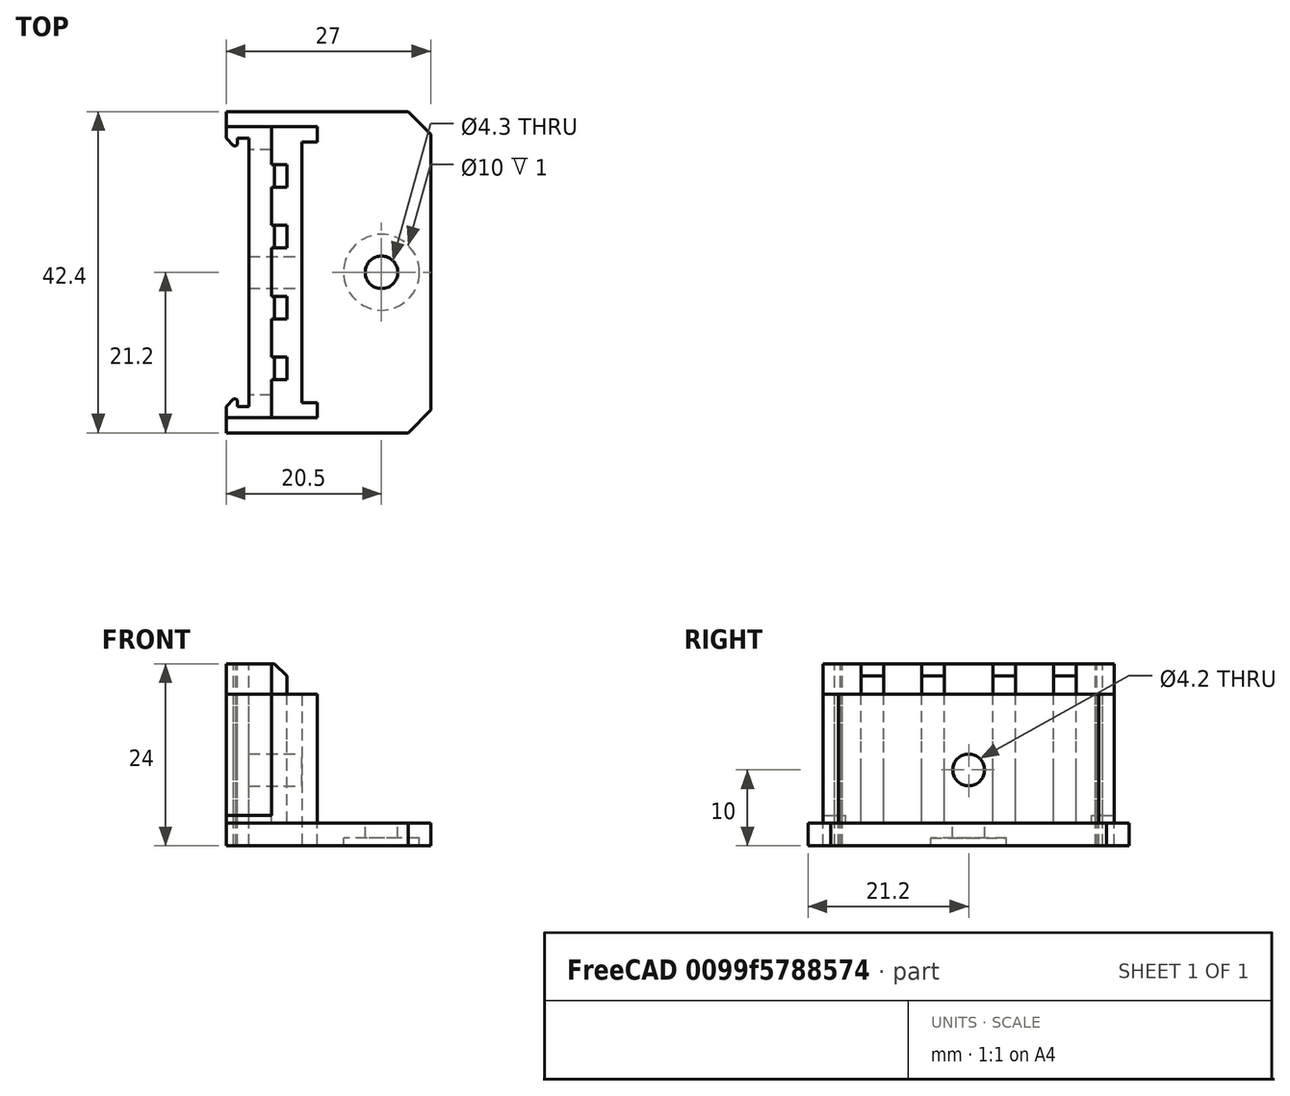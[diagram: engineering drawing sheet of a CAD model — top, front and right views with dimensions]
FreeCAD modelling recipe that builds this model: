
FCSTD DOCUMENT  (FreeCAD 0.18R16146 (Git))
Label: din-clip
License: All rights reserved
LicenseURL: http://en.wikipedia.org/wiki/All_rights_reserved
objects: Part::Box×15, Part::Chamfer×6, Part::Feature×5, Part::MultiFuse×4, Part::Cut×4, Part::Cylinder×3
note: 37 computed .brp shape members not serialized (recipe doc carries the construction recipe); baked Part::Feature solids carry a one-line shape summary decoded from their .brp

FEATURE [Part::Box] Box  label="Cube"
  AttacherType = Attacher::AttachEngine3D
  Height = 10
  Length = 3
  Width = 35.4
FEATURE [Part::Box] Box001  label="Cube001"
  AttacherType = Attacher::AttachEngine3D
  Height = 10
  Length = 6
  Placement = pos=(-3,-1.5,0) rot=(0,0,1;0rad)
  Width = 1.5
FEATURE [Part::Box] Box002  label="Cube002"
  AttacherType = Attacher::AttachEngine3D
  Height = 10
  Length = 6
  Placement = pos=(-3,35.4,0) rot=(0,0,1;0rad)
  Width = 1.5
FEATURE [Part::Box] Box003  label="Cube003"
  AttacherType = Attacher::AttachEngine3D
  Height = 10
  Length = 1.5
  Placement = pos=(-3,-1.5,0) rot=(0,0,1;0rad)
  Width = 2.5
FEATURE [Part::Box] Box004  label="Cube004"
  AttacherType = Attacher::AttachEngine3D
  Height = 10
  Length = 1.5
  Placement = pos=(-3,34.4,0) rot=(0,0,1;0rad)
  Width = 2.5
FEATURE [Part::Chamfer] Chamfer
  Base = -> Box004
  Edges = 1 edges r=1: [Edge1]
FEATURE [Part::Chamfer] Chamfer001
  Base = -> Box003
  Edges = 1 edges r=1: [Edge3]
FEATURE [Part::Chamfer] Chamfer002
  Base = -> Chamfer
  Edges = 1 edges r=0.2: [Edge15]
FEATURE [Part::Chamfer] Chamfer003
  Base = -> Chamfer001
  Edges = 1 edges r=0.2: [Edge15]
FEATURE [Part::MultiFuse] Fusion
  Placement = pos=(0,0,4) rot=(0,0,1;0rad)
  Shapes = -> [Chamfer003,Chamfer002,Box002,Box001,Box]
FEATURE [Part::Box] Box005  label="Cube005"
  AttacherType = Attacher::AttachEngine3D
  Height = 3
  Length = 27
  Placement = pos=(-3,-3.5,0) rot=(0,0,1;0rad)
  Width = 42.4
FEATURE [Part::Box] Box006  label="Cube006"
  AttacherType = Attacher::AttachEngine3D
  Height = 4
  Length = 3
  Placement = pos=(0,1.5,0) rot=(0,0,1;0rad)
  Width = 32.4
FEATURE [Part::Box] Box007  label="Cube007"
  AttacherType = Attacher::AttachEngine3D
  Height = 4
  Length = 3
  Placement = pos=(-3,0,0) rot=(0,0,1;0rad)
  Width = 35.4
FEATURE [Part::Cylinder] Cylinder
  Angle = 360
  AttacherType = Attacher::AttachEngine3D
  Height = 10
  Placement = pos=(17.5,17.7,0) rot=(0,0,1;0rad)
  Radius = 2.15
FEATURE [Part::Box] Box008  label="Cube008"
  AttacherType = Attacher::AttachEngine3D
  Height = 14
  Length = 2
  Placement = pos=(3,3.5,0) rot=(0,0,1;0rad)
  Width = 3
FEATURE [Part::Box] Box009  label="Cube009"
  AttacherType = Attacher::AttachEngine3D
  Height = 14
  Length = 2
  Placement = pos=(3,28.9,0) rot=(0,0,1;0rad)
  Width = 3
FEATURE [Part::Box] Box010  label="Cube010"
  AttacherType = Attacher::AttachEngine3D
  Height = 14
  Length = 2
  Placement = pos=(3,11.5,0) rot=(0,0,1;0rad)
  Width = 3
FEATURE [Part::Box] Box011  label="Cube011"
  AttacherType = Attacher::AttachEngine3D
  Height = 14
  Length = 2
  Placement = pos=(3,20.9,0) rot=(0,0,1;0rad)
  Width = 3
FEATURE [Part::Cut] Cut
  Base = -> Box005
  Tool = -> Box007
FEATURE [Part::Cut] Cut001
  Base = -> Cut
  Tool = -> Cylinder
FEATURE [Part::MultiFuse] Fusion001
  Shapes = -> [Box009,Box011,Box010,Box008]
FEATURE [Part::Feature] Fusion002
  Placement = pos=(0,0,14) rot=(0,0,1;0rad)
  shape: bbox 6 x 38.4 x 10 mm, 34 faces (baked)
FEATURE [Part::Feature] Fusion001001  label="Fusion003"
  Placement = pos=(0,0,10) rot=(0,0,1;0rad)
  shape: bbox 2 x 28.4 x 14 mm, 24 faces, 4 solids (baked)
FEATURE [Part::Chamfer] Chamfer004
  Base = -> Fusion001001
  Edges = 4 edges r=1.6: [Edge6,Edge18,Edge30,Edge42]
FEATURE [Part::Feature] Fusion002001  label="arm-clip"
  Placement = pos=(0,0,-14) rot=(0,0,1;0rad)
  shape: bbox 6 x 38.4 x 10 mm, 18 faces (baked)
FEATURE [Part::Chamfer] Chamfer005
  Base = -> Cut001
  Edges = 2 edges r=3: [Edge22,Edge23]
FEATURE [Part::MultiFuse] Fusion002002
  Shapes = -> [Chamfer005,Chamfer004,Fusion002,Fusion001,Box006,Fusion]
FEATURE [Part::Cylinder] Cylinder001
  Angle = 360
  AttacherType = Attacher::AttachEngine3D
  Height = 1
  Placement = pos=(17.5,17.7,0) rot=(0,0,1;0rad)
  Radius = 5
FEATURE [Part::Cut] Cut002  label="psu-mount"
  Base = -> Fusion002002
  Tool = -> Cylinder001
FEATURE [Part::Feature] Fusion002003  label="arm-clip001"
  Placement = pos=(0,0,-4) rot=(0,0,1;0rad)
  shape: bbox 6 x 38.4 x 10 mm, 18 faces (baked)
FEATURE [Part::Box] Box012  label="Cube012"
  AttacherType = Attacher::AttachEngine3D
  Height = 20
  Length = 7
  Placement = pos=(0,-1.5,0) rot=(0,0,1;0rad)
  Width = 38.4
FEATURE [Part::Box] Box013  label="Cube013"
  AttacherType = Attacher::AttachEngine3D
  Height = 20
  Length = 9
  Placement = pos=(0,-1.5,0) rot=(0,0,1;0rad)
  Width = 2
FEATURE [Part::Box] Box014  label="Cube014"
  AttacherType = Attacher::AttachEngine3D
  Height = 20
  Length = 9
  Placement = pos=(0,34.9,0) rot=(0,0,1;0rad)
  Width = 2
FEATURE [Part::Cylinder] Cylinder002
  Angle = 360
  AttacherType = Attacher::AttachEngine3D
  Height = 10
  Placement = pos=(-2.2e-15,17.7,10) rot=(0,1,0;1.5708rad)
  Radius = 2.1
FEATURE [Part::MultiFuse] Fusion002004
  Shapes = -> [Box014,Box013,Box012,Fusion002003,Fusion002001]
FEATURE [Part::Cut] Cut003
  Base = -> Fusion002004
  Tool = -> Cylinder002
FEATURE [Part::Feature] Cut003001  label="din-mount"
  shape: bbox 12 x 38.4 x 20 mm, 68 faces (baked)
